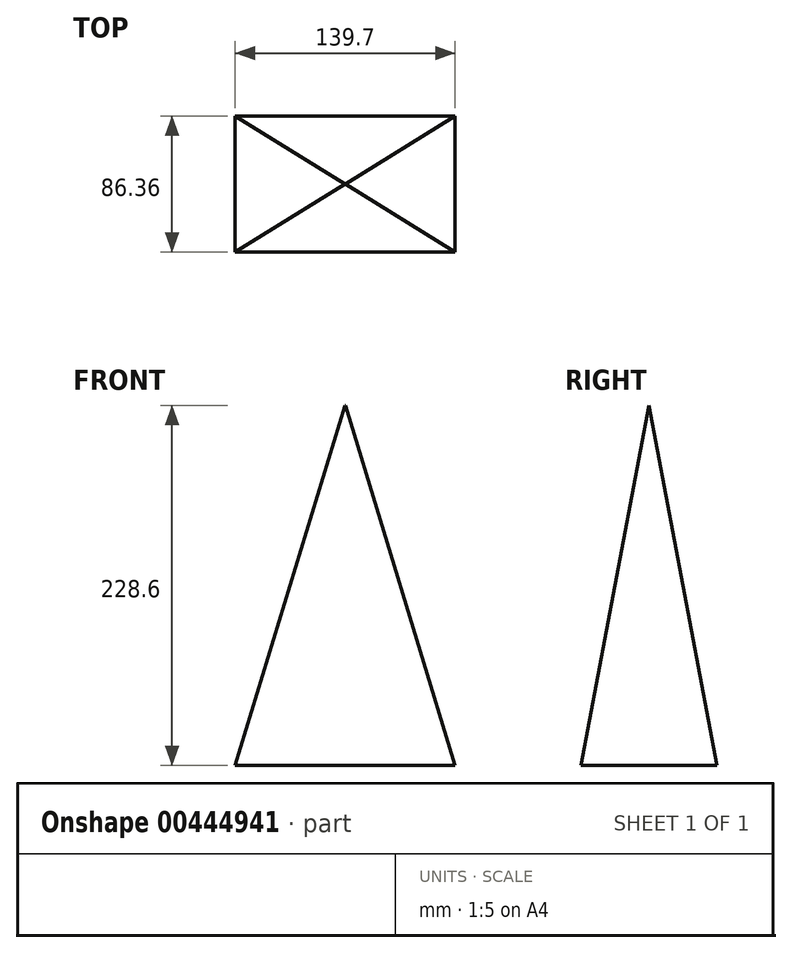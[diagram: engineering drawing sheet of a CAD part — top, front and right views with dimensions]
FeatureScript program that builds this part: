
annotation { "Feature Type Name" : "Feature", "Feature Type Description" : "" }
export const myFeature = defineFeature(function(context is Context, id is Id, definition is map)
    precondition{}
    {
        {
            var Q0;
            Q0=qCreatedBy(makeId("Top.planeOp"),FACE);
            var sketch = newSketch(context, id + "F0", { "sketchPlane" : qUnion([Q0])});
            skLineSegment(sketch, "E0.bottom", {"start": v(-69.85, 43.18) * mm, "end": v(69.85, 43.18) * mm});
            skLineSegment(sketch, "E0.top", {"start": v(-69.85, -43.18) * mm, "end": v(69.85, -43.18) * mm});
            skLineSegment(sketch, "E0.left", {"start": v(-69.85, 43.18) * mm, "end": v(-69.85, -43.18) * mm});
            skLineSegment(sketch, "E0.right", {"start": v(69.85, 43.18) * mm, "end": v(69.85, -43.18) * mm});
            skSolve(sketch);
        }
        {
            var Q0;
            Q0=makeQuery(id+"F0.imprint","IMPRINT",FACE,{"disambiguationData":[TD([[makeQuery(id+"F0.imprint","IMPRINT",EDGE,{"derivedFrom":sQuery(id+"F0.wireOp",EDGE,"E0.bottom")}),-1.0]])]});
            extrude(context, id + "F1", {"entities" : qUnion([Q0]), "depth" : 228.6 * mm});
        }
        {
            var Q0;
            Q0=makeQuery(id+"F1.opExtrude","CAP_EDGE",EDGE,{"disambiguationData":[OSD([sQuery(id+"F0.wireOp",EDGE,"E0.right")])],"isStart":false});
            var Q1;
            Q1=makeQuery(id+"F1.opExtrude","CAP_EDGE",EDGE,{"disambiguationData":[OSD([sQuery(id+"F0.wireOp",EDGE,"E0.left")])],"isStart":false});
            chamfer(context, id + "F2", {"entities" : qUnion([Q0, Q1]), "chamferType" : ChamferType.TWO_OFFSETS, "width1" : 228.6 * mm, "oppositeDirection" : false, "width2" : 69.72 * mm, "tangentPropagation" : true});
        }
        {
            var Q0;
            Q0=makeQuery(id+"F1.opExtrude","CAP_EDGE",EDGE,{"disambiguationData":[OSD([sQuery(id+"F0.wireOp",EDGE,"E0.top")])],"isStart":false});
            var Q1;
            Q1=makeQuery(id+"F1.opExtrude","CAP_EDGE",EDGE,{"disambiguationData":[OSD([sQuery(id+"F0.wireOp",EDGE,"E0.bottom")])],"isStart":false});
            chamfer(context, id + "F3", {"entities" : qUnion([Q0, Q1]), "chamferType" : ChamferType.TWO_OFFSETS, "width1" : 43.18 * mm, "oppositeDirection" : false, "width2" : 228.6 * mm, "tangentPropagation" : true});
        }
    });
